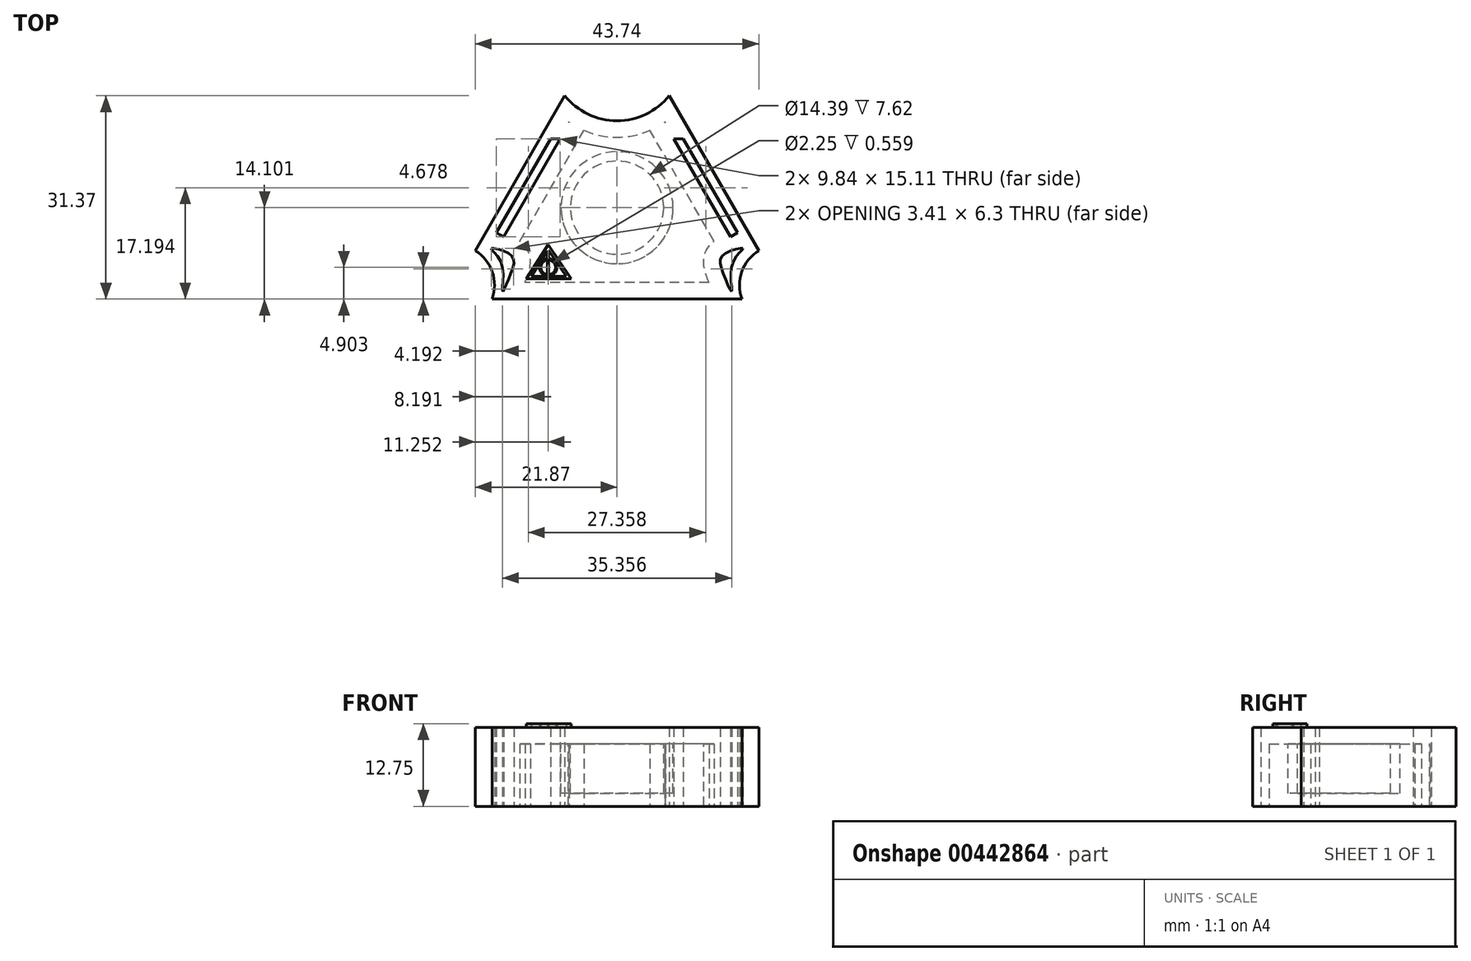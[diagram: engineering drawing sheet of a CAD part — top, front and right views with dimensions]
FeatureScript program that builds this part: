
annotation { "Feature Type Name" : "Feature", "Feature Type Description" : "" }
export const myFeature = defineFeature(function(context is Context, id is Id, definition is map)
    precondition{}
    {
        {
            var Q0;
            Q0=qCreatedBy(makeId("Top.planeOp"),FACE);
            var sketch = newSketch(context, id + "F0", { "sketchPlane" : qUnion([Q0])});
            skLineSegment(sketch, "E0", {"start": v(0, -24.75) * mm, "end": v(-19.28, -24.75) * mm});
            skArc(sketch, "E1", {"start": v(-19.28, -24.75) * mm, "mid": v(-19.24, -20.55) * mm, "end": v(-21.87, -17.27) * mm});
            skLineSegment(sketch, "E2", {"start": v(-21.87, -17.27) * mm, "end": v(-8.06, 6.62) * mm});
            skLineSegment(sketch, "E3.MirrorCS", {"start": v(21.87, -17.27) * mm, "end": v(8.06, 6.62) * mm});
            skArc(sketch, "E4.MirrorCS", {"start": v(19.28, -24.75) * mm, "mid": v(19.24, -20.55) * mm, "end": v(21.87, -17.27) * mm});
            skLineSegment(sketch, "E5.MirrorCS", {"start": v(0, -24.75) * mm, "end": v(19.28, -24.75) * mm});
            skArc(sketch, "E6", {"start": v(-8.06, 6.62) * mm, "mid": v(0, 2.78) * mm, "end": v(8.06, 6.62) * mm});
            skLineSegment(sketch, "E7", {"start": v(-10.23, 0) * mm, "end": v(-18.6, -14.48) * mm});
            skLineSegment(sketch, "E8", {"start": v(-18.6, -14.48) * mm, "end": v(-17.5, -15.11) * mm});
            skLineSegment(sketch, "E9", {"start": v(-17.5, -15.11) * mm, "end": v(-8.76, 0) * mm});
            skLineSegment(sketch, "E10", {"start": v(-8.76, 0) * mm, "end": v(-10.23, 0) * mm});
            skFitSpline(sketch, "E11", {"points": [v(-19.38, -16.92) * mm, v(-17.84, -19.15) * mm, v(-17.67, -23.51) * mm, v(-16.3, -20.6) * mm, v(-16.39, -17.95) * mm, v(-19.38, -16.92) * mm]});
            skLineSegment(sketch, "E12", {"start": v(0, 5.15) * mm, "end": v(0, -28.39) * mm, "construction": true});
            skPoint(sketch, "E12.startSnap0", {"position": v(0, 2.78) * mm});
            skLineSegment(sketch, "E13.MirrorCS", {"start": v(17.5, -15.11) * mm, "end": v(8.76, 0) * mm});
            skLineSegment(sketch, "E14.MirrorCS", {"start": v(10.23, 0) * mm, "end": v(18.6, -14.48) * mm});
            skLineSegment(sketch, "E15.MirrorCS", {"start": v(8.76, 0) * mm, "end": v(10.23, 0) * mm});
            skLineSegment(sketch, "E16.MirrorCS", {"start": v(18.6, -14.48) * mm, "end": v(17.5, -15.11) * mm});
            skFitSpline(sketch, "E17.MirrorC", {"points": [v(19.38, -16.92) * mm, v(17.84, -19.15) * mm, v(17.67, -23.51) * mm, v(16.3, -20.6) * mm, v(16.39, -17.95) * mm, v(19.38, -16.92) * mm]});
            skSolve(sketch);
        }
        {
            var Q0;
            Q0 = qSketchRegion(id + "F0", true);
            extrude(context, id + "F1", {"entities" : qUnion([Q0]), "depth" : 12.2 * mm});
        }
        {
            var Q0;
            Q0=makeQuery(id+"F1.opExtrude","CAP_FACE",FACE,{"disambiguationData":[OSD([sQuery(id+"F0.wireOp",EDGE,"E0"),sQuery(id+"F0.wireOp",EDGE,"E1"),sQuery(id+"F0.wireOp",EDGE,"E2"),sQuery(id+"F0.wireOp",EDGE,"E3.MirrorCS"),sQuery(id+"F0.wireOp",EDGE,"E4.MirrorCS"),sQuery(id+"F0.wireOp",EDGE,"E5.MirrorCS"),sQuery(id+"F0.wireOp",EDGE,"E6")])],"isStart":true});
            shell(context, id + "F2", {"entities" : qUnion([Q0]), "thickness" : 2.54 * mm});
        }
        {
            var Q0;
            Q0=makeQuery(id+"F2.opShell","OFFSET_FACE",FACE,{"disambiguationData":[OSD([sQuery(id+"F0.wireOp",EDGE,"E0"),sQuery(id+"F0.wireOp",EDGE,"E1"),sQuery(id+"F0.wireOp",EDGE,"E2"),sQuery(id+"F0.wireOp",EDGE,"E3.MirrorCS"),sQuery(id+"F0.wireOp",EDGE,"E4.MirrorCS"),sQuery(id+"F0.wireOp",EDGE,"E5.MirrorCS"),sQuery(id+"F0.wireOp",EDGE,"E6")])]});
            var sketch = newSketch(context, id + "F3", { "sketchPlane" : qUnion([Q0])});
            skCircle(sketch, "E18", {"center": v(0, 10.65) * mm, "radius": 8.64 * mm});
            skCircle(sketch, "E19", {"center": v(0, 10.65) * mm, "radius": 7.2 * mm});
            skSolve(sketch);
        }
        {
            var Q0;
            Q0 = qSketchRegion(id + "F3", true);
            extrude(context, id + "F4", {"entities" : qUnion([Q0]), "operationType" : NewBodyOperationType.ADD, "depth" : 7.62 * mm});
        }
        {
            var Q0;
            Q0=makeQuery(id+"F1.opExtrude","CAP_FACE",FACE,{"disambiguationData":[OSD([sQuery(id+"F0.wireOp",EDGE,"E0"),sQuery(id+"F0.wireOp",EDGE,"E1"),sQuery(id+"F0.wireOp",EDGE,"E2"),sQuery(id+"F0.wireOp",EDGE,"E3.MirrorCS"),sQuery(id+"F0.wireOp",EDGE,"E4.MirrorCS"),sQuery(id+"F0.wireOp",EDGE,"E5.MirrorCS"),sQuery(id+"F0.wireOp",EDGE,"E6"),sQuery(id+"F0.wireOp",EDGE,"E7"),sQuery(id+"F0.wireOp",EDGE,"E8"),sQuery(id+"F0.wireOp",EDGE,"E9"),sQuery(id+"F0.wireOp",EDGE,"E10"),sQuery(id+"F0.wireOp",EDGE,"E11"),sQuery(id+"F0.wireOp",EDGE,"E13.MirrorCS"),sQuery(id+"F0.wireOp",EDGE,"E14.MirrorCS"),sQuery(id+"F0.wireOp",EDGE,"E15.MirrorCS"),sQuery(id+"F0.wireOp",EDGE,"E16.MirrorCS"),sQuery(id+"F0.wireOp",EDGE,"E17.MirrorC")])],"isStart":false});
            var sketch = newSketch(context, id + "F5", { "sketchPlane" : qUnion([Q0])});
            skLineSegment(sketch, "E20", {"start": v(-10.64, -17.08) * mm, "end": v(-13.22, -21.23) * mm});
            skLineSegment(sketch, "E21", {"start": v(-13.22, -21.23) * mm, "end": v(-7.83, -21.23) * mm});
            skLineSegment(sketch, "E22", {"start": v(-7.83, -21.23) * mm, "end": v(-10.64, -17.08) * mm});
            skLineSegment(sketch, "E23", {"start": v(-10.64, -16.35) * mm, "end": v(-7.06, -21.64) * mm});
            skLineSegment(sketch, "E24", {"start": v(-7.06, -21.64) * mm, "end": v(-13.97, -21.64) * mm});
            skLineSegment(sketch, "E25", {"start": v(-10.64, -16.35) * mm, "end": v(-13.97, -21.64) * mm});
            skSolve(sketch);
        }
        {
            var Q0;
            Q0 = qSketchRegion(id + "F5", true);
            extrude(context, id + "F6", {"entities" : qUnion([Q0]), "operationType" : NewBodyOperationType.ADD, "depth" : 0.53 * mm});
        }
        {
            var Q0;
            {var subQ0=sQuery(id+"F0.wireOp",EDGE,"E10");var subQ1=sQuery(id+"F0.wireOp",EDGE,"E9");var subQ2=sQuery(id+"F0.wireOp",EDGE,"E8");var subQ3=sQuery(id+"F0.wireOp",EDGE,"E7");var subQ4=sQuery(id+"F0.wireOp",EDGE,"E6");var subQ5=sQuery(id+"F0.wireOp",EDGE,"E4.MirrorCS");var subQ6=sQuery(id+"F0.wireOp",EDGE,"E5.MirrorCS");var subQ7=sQuery(id+"F0.wireOp",EDGE,"E0");var subQ8=sQuery(id+"F0.wireOp",EDGE,"E1");var subQ9=sQuery(id+"F0.wireOp",EDGE,"E2");var subQ10=sQuery(id+"F0.wireOp",EDGE,"E3.MirrorCS");var subQ11=sQuery(id+"F0.wireOp",EDGE,"E11");var subQ12=sQuery(id+"F0.wireOp",EDGE,"E13.MirrorCS");var subQ13=sQuery(id+"F0.wireOp",EDGE,"E14.MirrorCS");var subQ14=sQuery(id+"F0.wireOp",EDGE,"E15.MirrorCS");var subQ15=sQuery(id+"F0.wireOp",EDGE,"E16.MirrorCS");var subQ16=sQuery(id+"F0.wireOp",EDGE,"E17.MirrorC");Q0=makeQuery(id+"F6.boolean.opBoolean","SPLIT",FACE,{"disambiguationData":[TD([makeQuery(id+"F1.opExtrude","SWEPT_FACE",FACE,{"disambiguationData":[OSD([subQ8])]})])],"derivedFrom":makeQuery(id+"F1.opExtrude","CAP_FACE",FACE,{"disambiguationData":[OSD([subQ7,subQ8,subQ9,subQ10,subQ5,subQ6,subQ4,subQ3,subQ2,subQ1,subQ0,subQ11,subQ12,subQ13,subQ14,subQ15,subQ16])],"isStart":false})});}
            var sketch = newSketch(context, id + "F7", { "sketchPlane" : qUnion([Q0])});
            skLineSegment(sketch, "E26", {"start": v(-10.75, -17.04) * mm, "end": v(-10.75, -21.3) * mm});
            skLineSegment(sketch, "E27", {"start": v(-10.53, -17.04) * mm, "end": v(-10.53, -21.48) * mm});
            skLineSegment(sketch, "E28", {"start": v(-10.75, -17.04) * mm, "end": v(-10.53, -17.04) * mm});
            skLineSegment(sketch, "E29", {"start": v(-10.53, -21.48) * mm, "end": v(-10.75, -21.3) * mm});
            skSolve(sketch);
        }
        {
            var Q0;
            Q0 = qSketchRegion(id + "F7", true);
            extrude(context, id + "F8", {"entities" : qUnion([Q0]), "operationType" : NewBodyOperationType.ADD, "depth" : 0.53 * mm});
        }
        {
            var Q0;
            {var subQ0=sQuery(id+"F0.wireOp",EDGE,"E10");var subQ1=sQuery(id+"F0.wireOp",EDGE,"E9");var subQ2=sQuery(id+"F0.wireOp",EDGE,"E8");var subQ3=sQuery(id+"F0.wireOp",EDGE,"E7");var subQ4=sQuery(id+"F0.wireOp",EDGE,"E6");var subQ5=sQuery(id+"F0.wireOp",EDGE,"E4.MirrorCS");var subQ6=sQuery(id+"F0.wireOp",EDGE,"E5.MirrorCS");var subQ7=sQuery(id+"F0.wireOp",EDGE,"E0");var subQ8=sQuery(id+"F0.wireOp",EDGE,"E1");var subQ9=sQuery(id+"F0.wireOp",EDGE,"E2");var subQ10=sQuery(id+"F0.wireOp",EDGE,"E3.MirrorCS");var subQ11=sQuery(id+"F0.wireOp",EDGE,"E11");var subQ12=sQuery(id+"F0.wireOp",EDGE,"E13.MirrorCS");var subQ13=sQuery(id+"F0.wireOp",EDGE,"E14.MirrorCS");var subQ14=sQuery(id+"F0.wireOp",EDGE,"E15.MirrorCS");var subQ15=sQuery(id+"F0.wireOp",EDGE,"E16.MirrorCS");var subQ16=sQuery(id+"F0.wireOp",EDGE,"E17.MirrorC");Q0=makeQuery(id+"F6.boolean.opBoolean","SPLIT",FACE,{"disambiguationData":[TD([makeQuery(id+"F1.opExtrude","SWEPT_FACE",FACE,{"disambiguationData":[OSD([subQ8])]})])],"derivedFrom":makeQuery(id+"F1.opExtrude","CAP_FACE",FACE,{"disambiguationData":[OSD([subQ7,subQ8,subQ9,subQ10,subQ5,subQ6,subQ4,subQ3,subQ2,subQ1,subQ0,subQ11,subQ12,subQ13,subQ14,subQ15,subQ16])],"isStart":false})});}
            var sketch = newSketch(context, id + "F9", { "sketchPlane" : qUnion([Q0])});
            skCircle(sketch, "E30", {"center": v(-10.62, -19.85) * mm, "radius": 1.36 * mm});
            skCircle(sketch, "E31", {"center": v(-10.62, -19.85) * mm, "radius": 1.13 * mm});
            skSolve(sketch);
        }
        {
            var Q0;
            Q0 = qSketchRegion(id + "F9", true);
            extrude(context, id + "F10", {"entities" : qUnion([Q0]), "operationType" : NewBodyOperationType.ADD, "depth" : 0.56 * mm});
        }
    });
